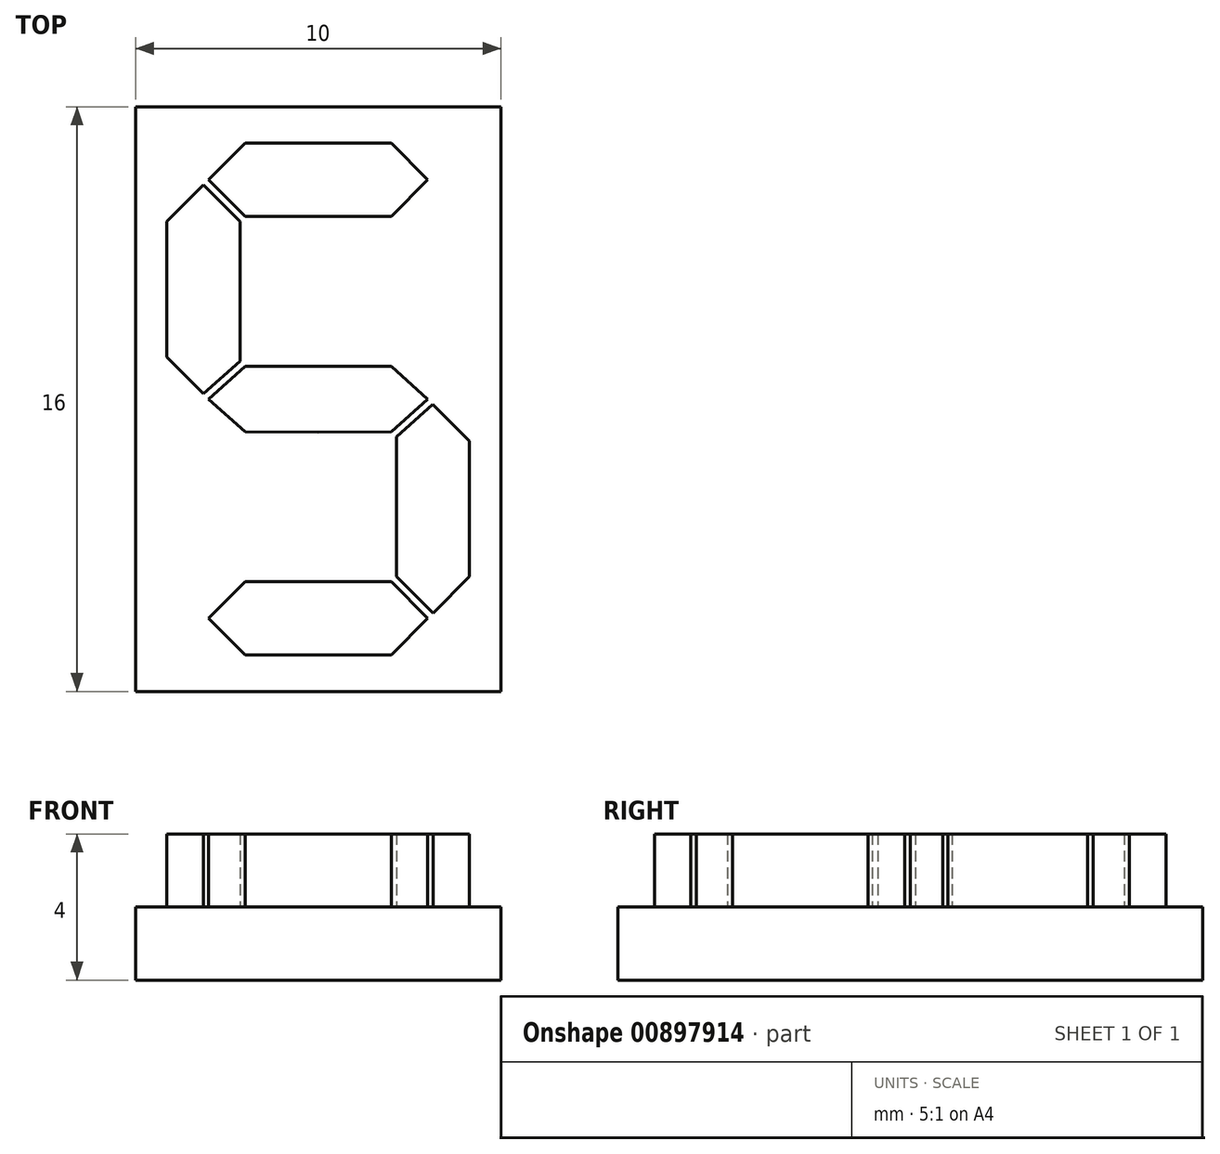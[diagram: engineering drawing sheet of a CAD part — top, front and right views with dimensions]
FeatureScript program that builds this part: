
annotation { "Feature Type Name" : "Feature", "Feature Type Description" : "" }
export const myFeature = defineFeature(function(context is Context, id is Id, definition is map)
    precondition{}
    {
        {
            var Q0;
            Q0=qCreatedBy(makeId("Top.planeOp"),FACE);
            var sketch = newSketch(context, id + "F0", { "sketchPlane" : qUnion([Q0])});
            skLineSegment(sketch, "E0.bottom", {"start": v(5, -8) * mm, "end": v(-5, -8) * mm});
            skLineSegment(sketch, "E0.top", {"start": v(5, 8) * mm, "end": v(-5, 8) * mm});
            skLineSegment(sketch, "E0.left", {"start": v(5, -8) * mm, "end": v(5, 8) * mm});
            skLineSegment(sketch, "E0.right", {"start": v(-5, -8) * mm, "end": v(-5, 8) * mm});
            skPoint(sketch, "E0.middle", {"position": v(0, 0) * mm});
            skSolve(sketch);
        }
        {
            var Q0;
            Q0=makeQuery(id+"F0.imprint","IMPRINT",FACE,{"disambiguationData":[TD([[makeQuery(id+"F0.imprint","IMPRINT",EDGE,{"derivedFrom":sQuery(id+"F0.wireOp",EDGE,"E0.bottom")}),-1.0]])]});
            extrude(context, id + "F1", {"entities" : qUnion([Q0]), "depth" : 2 * mm, "offsetDistance" : 25 * mm});
        }
        {
            var Q0;
            Q0=makeQuery(id+"F1.opExtrude","CAP_FACE",FACE,{"disambiguationData":[OSD([sQuery(id+"F0.wireOp",EDGE,"E0.bottom"),sQuery(id+"F0.wireOp",EDGE,"E0.top"),sQuery(id+"F0.wireOp",EDGE,"E0.left"),sQuery(id+"F0.wireOp",EDGE,"E0.right")])],"isStart":false});
            var sketch = newSketch(context, id + "F2", { "sketchPlane" : qUnion([Q0])});
            skLineSegment(sketch, "E1", {"start": v(-3, 8) * mm, "end": v(-3, -8) * mm, "construction": true});
            skLineSegment(sketch, "E2.0.1.0", {"start": v(-5, 6) * mm, "end": v(5, 6) * mm, "construction": true});
            skLineSegment(sketch, "E2.direction2", {"start": v(-5, 7) * mm, "end": v(-5, 6) * mm, "construction": true});
            skLineSegment(sketch, "E3.1.0.0", {"start": v(-2, 8) * mm, "end": v(-2, -8) * mm, "construction": true});
            skLineSegment(sketch, "E3.3.0.0", {"start": v(0, 8) * mm, "end": v(0, -8) * mm, "construction": true});
            skLineSegment(sketch, "E3.direction1", {"start": v(-3, -8) * mm, "end": v(-2, -8) * mm, "construction": true});
            skLineSegment(sketch, "E4", {"start": v(-2, 7) * mm, "end": v(-3, 6) * mm});
            skLineSegment(sketch, "E5", {"start": v(-3, 6) * mm, "end": v(-2, 5) * mm});
            skLineSegment(sketch, "E6", {"start": v(-2, 5) * mm, "end": v(0, 5) * mm});
            skLineSegment(sketch, "E7", {"start": v(-2, 7) * mm, "end": v(0, 7) * mm});
            skLineSegment(sketch, "E8.0", {"start": v(-3.14, 5.86) * mm, "end": v(-2.14, 4.86) * mm});
            skLineSegment(sketch, "E9", {"start": v(-2.14, 4.86) * mm, "end": v(-2.14, 1.03) * mm});
            skLineSegment(sketch, "E10.0", {"start": v(-4.14, 4.86) * mm, "end": v(-4.14, 1.15) * mm});
            skLineSegment(sketch, "E11", {"start": v(-3.14, 5.86) * mm, "end": v(-4.14, 4.86) * mm});
            skLineSegment(sketch, "E12", {"start": v(-4.14, 4.86) * mm, "end": v(5, 4.86) * mm, "construction": true});
            skLineSegment(sketch, "E13", {"start": v(0, 0.9) * mm, "end": v(-2, 0.9) * mm});
            skLineSegment(sketch, "E14", {"start": v(-2, 0.9) * mm, "end": v(-3, 0) * mm});
            skLineSegment(sketch, "E15.0", {"start": v(-2.14, 1.03) * mm, "end": v(-3.14, 0.15) * mm});
            skLineSegment(sketch, "E16", {"start": v(-3.14, 5.86) * mm, "end": v(-3.14, 0.15) * mm, "construction": true});
            skLineSegment(sketch, "E17", {"start": v(-4.14, 1.15) * mm, "end": v(-3.14, 0.15) * mm});
            skLineSegment(sketch, "E18.MirrorCS", {"start": v(0, -0.9) * mm, "end": v(-2, -0.9) * mm});
            skLineSegment(sketch, "E19.MirrorCS", {"start": v(-2, -0.9) * mm, "end": v(-3, 0) * mm});
            skLineSegment(sketch, "E20.MirrorCS", {"start": v(-2, -5) * mm, "end": v(0, -5) * mm});
            skLineSegment(sketch, "E21.MirrorCS", {"start": v(-3, -6) * mm, "end": v(-2, -5) * mm});
            skLineSegment(sketch, "E22.MirrorCS", {"start": v(-2, -7) * mm, "end": v(-3, -6) * mm});
            skLineSegment(sketch, "E23.MirrorCS", {"start": v(-2, -7) * mm, "end": v(0, -7) * mm});
            skLineSegment(sketch, "E24.MirrorCS", {"start": v(-2.14, -4.86) * mm, "end": v(-2.14, -1.03) * mm});
            skLineSegment(sketch, "E25.MirrorCS", {"start": v(2, 7) * mm, "end": v(0, 7) * mm});
            skLineSegment(sketch, "E26.MirrorCS", {"start": v(2, 7) * mm, "end": v(3, 6) * mm});
            skLineSegment(sketch, "E27.MirrorCS", {"start": v(3, 6) * mm, "end": v(2, 5) * mm});
            skLineSegment(sketch, "E28.MirrorCS", {"start": v(2, 5) * mm, "end": v(0, 5) * mm});
            skLineSegment(sketch, "E29.MirrorCS", {"start": v(2, 0.9) * mm, "end": v(3, 0) * mm});
            skLineSegment(sketch, "E30.MirrorCS", {"start": v(0, 0.9) * mm, "end": v(2, 0.9) * mm});
            skLineSegment(sketch, "E31.MirrorCS", {"start": v(2, -0.9) * mm, "end": v(3, 0) * mm});
            skLineSegment(sketch, "E32.MirrorCS", {"start": v(0, -0.9) * mm, "end": v(2, -0.9) * mm});
            skLineSegment(sketch, "E33.MirrorCS", {"start": v(2.14, -1.03) * mm, "end": v(3.14, -0.15) * mm});
            skLineSegment(sketch, "E34.MirrorCS", {"start": v(4.14, -1.15) * mm, "end": v(3.14, -0.15) * mm});
            skLineSegment(sketch, "E35.MirrorCS", {"start": v(4.14, -4.86) * mm, "end": v(4.14, -1.15) * mm});
            skLineSegment(sketch, "E36.MirrorCS", {"start": v(2.14, -4.86) * mm, "end": v(2.14, -1.03) * mm});
            skLineSegment(sketch, "E37.MirrorCS", {"start": v(3.14, -5.86) * mm, "end": v(2.14, -4.86) * mm});
            skLineSegment(sketch, "E38.MirrorCS", {"start": v(3.14, -5.86) * mm, "end": v(4.14, -4.86) * mm});
            skLineSegment(sketch, "E39.MirrorCS", {"start": v(3, -6) * mm, "end": v(2, -5) * mm});
            skLineSegment(sketch, "E40.MirrorCS", {"start": v(2, -5) * mm, "end": v(0, -5) * mm});
            skLineSegment(sketch, "E41.MirrorCS", {"start": v(2, -7) * mm, "end": v(3, -6) * mm});
            skLineSegment(sketch, "E42.MirrorCS", {"start": v(2, -7) * mm, "end": v(0, -7) * mm});
            skSolve(sketch);
        }
        {
            var Q0;
            Q0=qSketchRegion(id+"F2",true);
            extrude(context, id + "F3", {"entities" : qUnion([Q0]), "operationType" : NewBodyOperationType.ADD, "depth" : 2 * mm, "offsetDistance" : 25 * mm});
        }
    });
